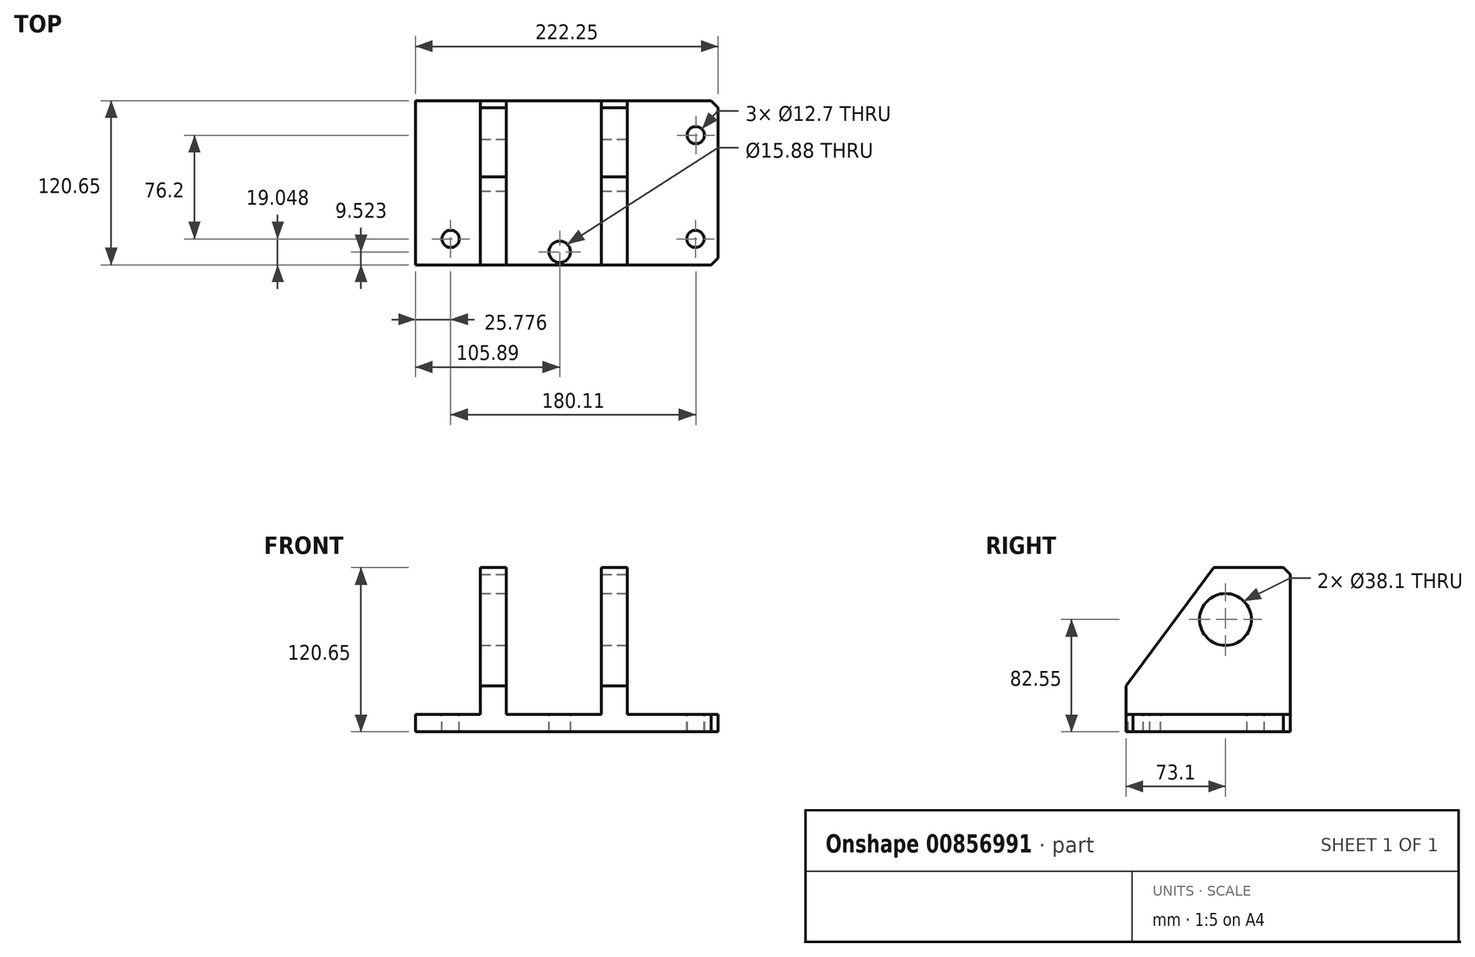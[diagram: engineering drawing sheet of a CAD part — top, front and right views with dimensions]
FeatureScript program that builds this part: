
annotation { "Feature Type Name" : "Feature", "Feature Type Description" : "" }
export const myFeature = defineFeature(function(context is Context, id is Id, definition is map)
    precondition{}
    {
        {
            var Q0;
            Q0=qCreatedBy(makeId("Top.planeOp"),FACE);
            var sketch = newSketch(context, id + "F0", { "sketchPlane" : qUnion([Q0])});
            skLineSegment(sketch, "E0.bottom", {"start": v(-105.9, -97.3) * mm, "end": v(116.36, -97.3) * mm});
            skLineSegment(sketch, "E0.top", {"start": v(-105.9, 23.35) * mm, "end": v(116.36, 23.35) * mm});
            skLineSegment(sketch, "E0.left", {"start": v(-105.9, -97.3) * mm, "end": v(-105.9, 23.35) * mm});
            skLineSegment(sketch, "E0.right", {"start": v(116.36, -97.3) * mm, "end": v(116.36, 23.35) * mm});
            skSolve(sketch);
        }
        {
            var Q0;
            Q0 = qSketchRegion(id + "F0", true);
            extrude(context, id + "F1", {"entities" : qUnion([Q0]), "depth" : 12.7 * mm, "offsetDistance" : 25.4 * mm});
        }
        {
            var Q0;
            Q0=makeQuery(id+"F1.opExtrude","CAP_FACE",FACE,{"disambiguationData":[OSD([sQuery(id+"F0.wireOp",EDGE,"E0.bottom"),sQuery(id+"F0.wireOp",EDGE,"E0.top"),sQuery(id+"F0.wireOp",EDGE,"E0.left"),sQuery(id+"F0.wireOp",EDGE,"E0.right")])],"isStart":false});
            var sketch = newSketch(context, id + "F2", { "sketchPlane" : qUnion([Q0])});
            skLineSegment(sketch, "E1", {"start": v(-58.27, -85.18) * mm, "end": v(-58.27, -97.3) * mm});
            skLineSegment(sketch, "E2", {"start": v(-58.27, -85.18) * mm, "end": v(-58.27, 23.35) * mm});
            skLineSegment(sketch, "E3", {"start": v(-39.22, -97.3) * mm, "end": v(-39.22, 23.35) * mm});
            skSolve(sketch);
        }
        {
            var Q0;
            {var subQ0=sQuery(id+"F2.wireOp",EDGE,"E1");Q0=makeQuery(id+"F2.imprint","IMPRINT",FACE,{"disambiguationData":[TD([[makeQuery(id+"F2.imprint","IMPRINT",EDGE,{"derivedFrom":subQ0}),1.0]])]});}
            extrude(context, id + "F3", {"entities" : qUnion([Q0]), "operationType" : NewBodyOperationType.ADD, "depth" : 107.95 * mm, "offsetDistance" : 25.4 * mm});
        }
        {
            var Q0;
            {var subQ0=sQuery(id+"F0.wireOp",EDGE,"E0.top");var subQ1=sQuery(id+"F0.wireOp",EDGE,"E0.right");var subQ2=sQuery(id+"F0.wireOp",EDGE,"E0.bottom");Q0=makeQuery(id+"F3.boolean.opBoolean","SPLIT",FACE,{"disambiguationData":[TD([makeQuery(id+"F1.opExtrude","SWEPT_FACE",FACE,{"disambiguationData":[OSD([subQ1])]})])],"derivedFrom":makeQuery(id+"F1.opExtrude","CAP_FACE",FACE,{"disambiguationData":[OSD([subQ2,subQ0,sQuery(id+"F0.wireOp",EDGE,"E0.left"),subQ1])],"isStart":false})});}
            var sketch = newSketch(context, id + "F4", { "sketchPlane" : qUnion([Q0])});
            skLineSegment(sketch, "E4", {"start": v(30.63, -84.24) * mm, "end": v(30.63, -97.3) * mm});
            skLineSegment(sketch, "E5", {"start": v(30.63, -97.3) * mm, "end": v(30.63, 23.35) * mm});
            skLineSegment(sketch, "E6", {"start": v(49.68, -97.3) * mm, "end": v(49.68, 23.35) * mm});
            skLineSegment(sketch, "E7", {"start": v(30.63, -97.3) * mm, "end": v(49.68, -97.3) * mm});
            skLineSegment(sketch, "E8", {"start": v(30.63, 23.35) * mm, "end": v(49.68, 23.35) * mm});
            skSolve(sketch);
        }
        {
            var Q0;
            Q0 = qSketchRegion(id + "F4", true);
            extrude(context, id + "F5", {"entities" : qUnion([Q0]), "operationType" : NewBodyOperationType.ADD, "depth" : 107.95 * mm, "offsetDistance" : 25.4 * mm});
        }
        {
            var Q0;
            Q0=makeQuery(id+"F5.opExtrude","CAP_EDGE",EDGE,{"disambiguationData":[OSD([sQuery(id+"F4.wireOp",EDGE,"E8")])],"isStart":false});
            chamfer(context, id + "F6", {"entities" : qUnion([Q0]), "chamferType" : ChamferType.TWO_OFFSETS, "width1" : 5.08 * mm, "oppositeDirection" : false, "width2" : 5.08 * mm, "tangentPropagation" : true});
        }
        {
            var Q0;
            Q0=makeQuery(id+"F5.opExtrude","SWEPT_FACE",FACE,{"disambiguationData":[OSD([sQuery(id+"F4.wireOp",EDGE,"E6")])]});
            var sketch = newSketch(context, id + "F7", { "sketchPlane" : qUnion([Q0])});
            skCircle(sketch, "E9", {"center": v(-24.2, 82.55) * mm, "radius": 19.05 * mm});
            skSolve(sketch);
        }
        {
            var Q0;
            Q0 = qSketchRegion(id + "F7", true);
            extrude(context, id + "F8", {"entities" : qUnion([Q0]), "operationType" : NewBodyOperationType.REMOVE, "oppositeDirection" : true, "depth" : 192.28 * mm, "offsetDistance" : 25.4 * mm});
        }
        {
            var Q0;
            Q0=makeQuery(id+"F3.opExtrude","CAP_EDGE",EDGE,{"disambiguationData":[OSD([sQuery(id+"F0.wireOp",EDGE,"E0.top")])],"isStart":false});
            chamfer(context, id + "F9", {"entities" : qUnion([Q0]), "width" : 5.08 * mm, "tangentPropagation" : true});
        }
        {
            var Q0;
            Q0=makeQuery(id+"F1.opExtrude","SWEPT_EDGE",EDGE,{"disambiguationData":[OSD([sQuery(id+"F0.wireOp",EDGE,"E0.bottom"),sQuery(id+"F0.wireOp",EDGE,"E0.right")])]});
            chamfer(context, id + "F10", {"entities" : qUnion([Q0]), "width" : 5.08 * mm, "tangentPropagation" : true});
        }
        {
            var Q0;
            Q0=makeQuery(id+"F1.opExtrude","SWEPT_EDGE",EDGE,{"disambiguationData":[OSD([sQuery(id+"F0.wireOp",EDGE,"E0.top"),sQuery(id+"F0.wireOp",EDGE,"E0.right")])]});
            chamfer(context, id + "F11", {"entities" : qUnion([Q0]), "width" : 5.08 * mm, "tangentPropagation" : true});
        }
        {
            var Q0;
            {var subQ0=sQuery(id+"F0.wireOp",EDGE,"E0.left");var subQ1=sQuery(id+"F0.wireOp",EDGE,"E0.top");var subQ2=sQuery(id+"F0.wireOp",EDGE,"E0.bottom");Q0=makeQuery(id+"F3.boolean.opBoolean","SPLIT",FACE,{"disambiguationData":[TD([makeQuery(id+"F1.opExtrude","SWEPT_FACE",FACE,{"disambiguationData":[OSD([subQ0])]})])],"derivedFrom":makeQuery(id+"F1.opExtrude","CAP_FACE",FACE,{"disambiguationData":[OSD([subQ2,subQ1,subQ0,sQuery(id+"F0.wireOp",EDGE,"E0.right")])],"isStart":false})});}
            var sketch = newSketch(context, id + "F12", { "sketchPlane" : qUnion([Q0])});
            skCircle(sketch, "E10", {"center": v(99.72, -78.25) * mm, "radius": 6.35 * mm});
            skCircle(sketch, "E11", {"center": v(100, -2.05) * mm, "radius": 6.35 * mm});
            skCircle(sketch, "E12", {"center": v(-80.11, -78.25) * mm, "radius": 6.35 * mm});
            skCircle(sketch, "E13", {"center": v(0, -87.78) * mm, "radius": 7.94 * mm});
            skSolve(sketch);
        }
        {
            var Q0;
            Q0 = qSketchRegion(id + "F12", true);
            extrude(context, id + "F13", {"entities" : qUnion([Q0]), "operationType" : NewBodyOperationType.REMOVE, "oppositeDirection" : true, "depth" : 25.4 * mm, "offsetDistance" : 25.4 * mm});
        }
        {
            var Q0;
            Q0=makeQuery(id+"F5.opExtrude","SWEPT_FACE",FACE,{"disambiguationData":[OSD([sQuery(id+"F4.wireOp",EDGE,"E6")])]});
            var sketch = newSketch(context, id + "F14", { "sketchPlane" : qUnion([Q0])});
            skLineSegment(sketch, "E14", {"start": v(-97.3, 33.73) * mm, "end": v(-32.77, 120.65) * mm});
            skLineSegment(sketch, "E15", {"start": v(-32.77, 120.65) * mm, "end": v(-97.3, 120.65) * mm});
            skLineSegment(sketch, "E16", {"start": v(-97.3, 120.65) * mm, "end": v(-97.3, 33.73) * mm});
            skSolve(sketch);
        }
        {
            var Q0;
            Q0 = qSketchRegion(id + "F14", true);
            extrude(context, id + "F15", {"entities" : qUnion([Q0]), "operationType" : NewBodyOperationType.REMOVE, "oppositeDirection" : true, "depth" : 216.15 * mm, "offsetDistance" : 25.4 * mm});
        }
    });
